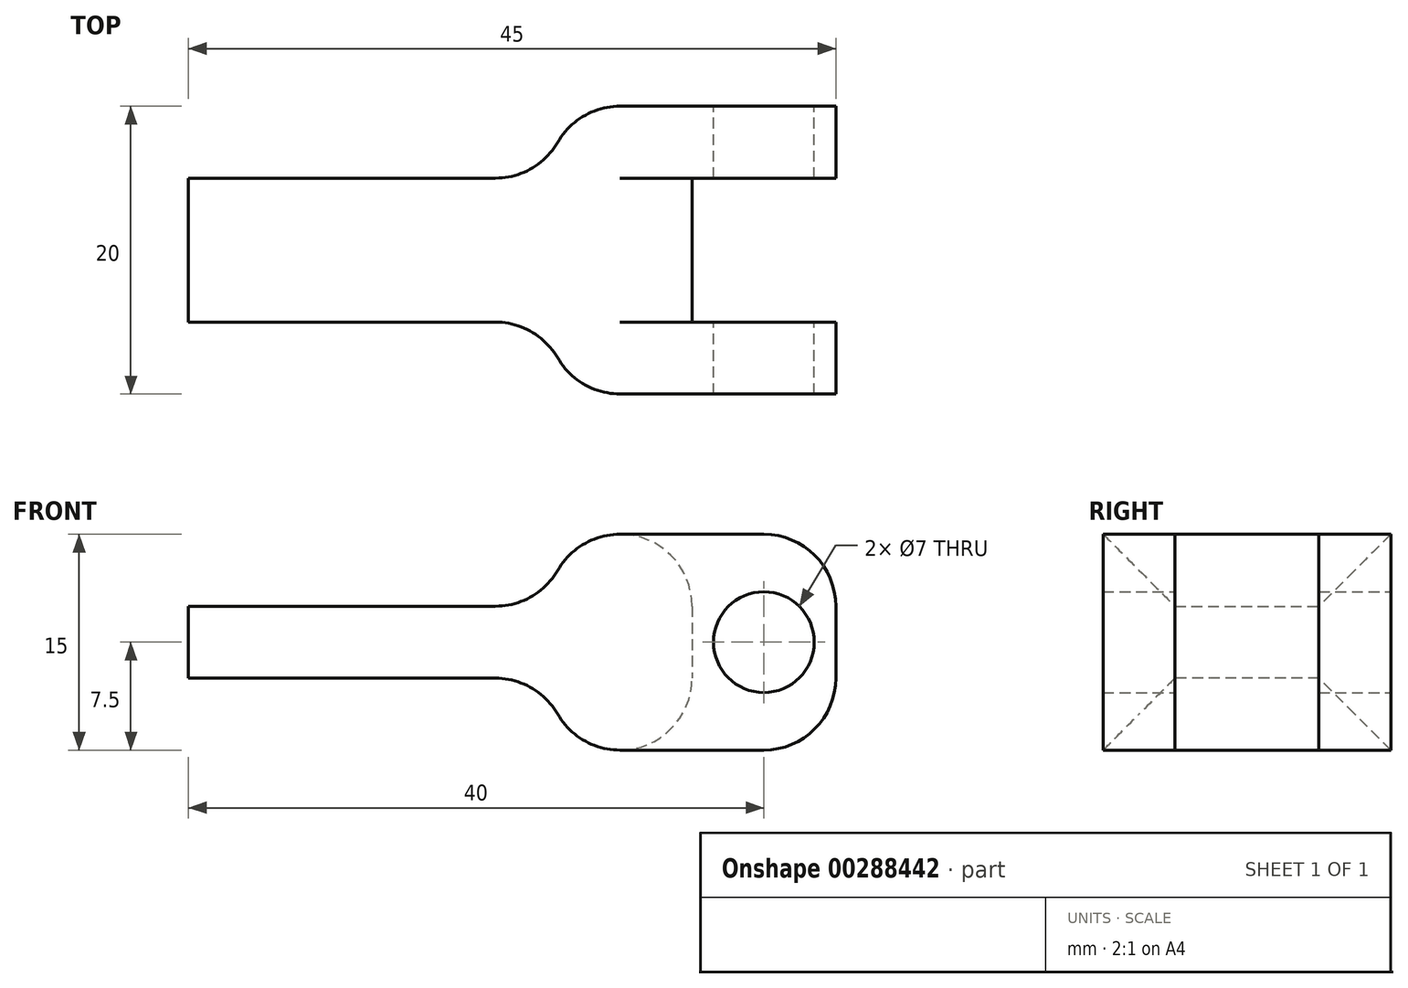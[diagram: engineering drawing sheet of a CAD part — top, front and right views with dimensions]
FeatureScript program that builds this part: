
annotation { "Feature Type Name" : "Feature", "Feature Type Description" : "" }
export const myFeature = defineFeature(function(context is Context, id is Id, definition is map)
    precondition{}
    {
        {
            var Q0;
            Q0=qCreatedBy(makeId("Top.planeOp"),FACE);
            var sketch = newSketch(context, id + "F0", { "sketchPlane" : qUnion([Q0])});
            skLineSegment(sketch, "E0.bottom", {"start": v(-10, 10) * mm, "end": v(10, 10) * mm});
            skLineSegment(sketch, "E0.top", {"start": v(-10, -10) * mm, "end": v(10, -10) * mm});
            skLineSegment(sketch, "E0.left", {"start": v(-10, 10) * mm, "end": v(-10, -10) * mm});
            skLineSegment(sketch, "E0.right", {"start": v(10, 10) * mm, "end": v(10, 5) * mm});
            skPoint(sketch, "E0.middle", {"position": v(0, 0) * mm});
            skLineSegment(sketch, "E1.bottom", {"start": v(0, -5) * mm, "end": v(10, -5) * mm});
            skLineSegment(sketch, "E1.top", {"start": v(0, 5) * mm, "end": v(10, 5) * mm});
            skLineSegment(sketch, "E1.left", {"start": v(0, -5) * mm, "end": v(0, 5) * mm});
            skPoint(sketch, "E1.middle", {"position": v(10, 0) * mm});
            skPoint(sketch, "E1.right.end.orphan", {"position": v(20, 5) * mm});
            skPoint(sketch, "E2.orphan", {"position": v(20, -5) * mm});
            skLineSegment(sketch, "E3.trimOffspring", {"start": v(10, -5) * mm, "end": v(10, -10) * mm});
            skSolve(sketch);
        }
        {
            var Q0;
            Q0 = qSketchRegion(id + "F0", true);
            extrude(context, id + "F1", {"entities" : qUnion([Q0]), "endBound" : BoundingType.SYMMETRIC, "depth" : 15 * mm});
        }
        {
            var Q0;
            Q0=makeQuery(id+"F1.opExtrude","SWEPT_FACE",FACE,{"disambiguationData":[OSD([sQuery(id+"F0.wireOp",EDGE,"E0.bottom")])]});
            var sketch = newSketch(context, id + "F2", { "sketchPlane" : qUnion([Q0])});
            skLineSegment(sketch, "E4", {"start": v(0, 0) * mm, "end": v(-10, 0) * mm, "construction": true});
            skCircle(sketch, "E5", {"center": v(-5, 0) * mm, "radius": 3.5 * mm});
            skSolve(sketch);
        }
        {
            var Q0;
            Q0=sQuery(id+"F2.wireOp",VERTEX,"E5.center");
            var Q1;
            Q1=makeQuery(id+"F1.opExtrude","SWEPT_BODY",BODY,{"disambiguationData":[OSD([sQuery(id+"F0.wireOp",EDGE,"E0.bottom"),sQuery(id+"F0.wireOp",EDGE,"E0.top"),sQuery(id+"F0.wireOp",EDGE,"E0.left"),sQuery(id+"F0.wireOp",EDGE,"E0.right"),sQuery(id+"F0.wireOp",EDGE,"E1.bottom"),sQuery(id+"F0.wireOp",EDGE,"E1.top"),sQuery(id+"F0.wireOp",EDGE,"E1.left"),sQuery(id+"F0.wireOp",EDGE,"E3.trimOffspring")])]});
            hole(context, id + "F3", {"style" : HoleStyle.SIMPLE, "endStyle" : HoleEndStyle.THROUGH, "holeDiameter" : 7 * mm, "tappedDepth" : 12 * mm, "tapClearance" : 3, "locations" : qUnion([Q0]), "scope" : qUnion([Q1])});
        }
        {
            var Q0;
            Q0=makeQuery(id+"F1.opExtrude","CAP_EDGE",EDGE,{"disambiguationData":[OSD([sQuery(id+"F0.wireOp",EDGE,"E0.right")])],"isStart":false});
            var Q1;
            Q1=makeQuery(id+"F1.opExtrude","CAP_EDGE",EDGE,{"disambiguationData":[OSD([sQuery(id+"F0.wireOp",EDGE,"E0.right")])],"isStart":true});
            var Q2;
            Q2=makeQuery(id+"F1.opExtrude","CAP_EDGE",EDGE,{"disambiguationData":[OSD([sQuery(id+"F0.wireOp",EDGE,"E3.trimOffspring")])],"isStart":false});
            var Q3;
            Q3=makeQuery(id+"F1.opExtrude","CAP_EDGE",EDGE,{"disambiguationData":[OSD([sQuery(id+"F0.wireOp",EDGE,"E3.trimOffspring")])],"isStart":true});
            var Q4;
            Q4=makeQuery(id+"F1.opExtrude","SWEPT_FACE",FACE,{"disambiguationData":[OSD([sQuery(id+"F0.wireOp",EDGE,"E0.left")])]});
            fillet(context, id + "F4", {"entities" : qUnion([Q0, Q1, Q2, Q3, Q4]), "radius" : 5 * mm, "tangentPropagation" : true, "allowEdgeOverflow" : false});
        }
        {
            var Q0;
            Q0=makeQuery(id+"F1.opExtrude","CAP_EDGE",EDGE,{"disambiguationData":[OSD([sQuery(id+"F0.wireOp",EDGE,"E1.left")])],"isStart":false});
            var Q1;
            Q1=makeQuery(id+"F1.opExtrude","CAP_EDGE",EDGE,{"disambiguationData":[OSD([sQuery(id+"F0.wireOp",EDGE,"E1.left")])],"isStart":true});
            fillet(context, id + "F5", {"entities" : qUnion([Q0, Q1]), "radius" : 5 * mm, "tangentPropagation" : true, "allowEdgeOverflow" : false});
        }
        {
            var Q0;
            Q0=makeQuery(id+"F1.opExtrude","SWEPT_FACE",FACE,{"disambiguationData":[OSD([sQuery(id+"F0.wireOp",EDGE,"E0.left")])]});
            var sketch = newSketch(context, id + "F6", { "sketchPlane" : qUnion([Q0])});
            skLineSegment(sketch, "E6.bottom", {"start": v(5, 2.5) * mm, "end": v(-5, 2.5) * mm});
            skLineSegment(sketch, "E6.top", {"start": v(5, -2.5) * mm, "end": v(-5, -2.5) * mm});
            skLineSegment(sketch, "E6.left", {"start": v(5, 2.5) * mm, "end": v(5, -2.5) * mm});
            skLineSegment(sketch, "E6.right", {"start": v(-5, 2.5) * mm, "end": v(-5, -2.5) * mm});
            skPoint(sketch, "E6.middle", {"position": v(0, 0) * mm});
            skSolve(sketch);
        }
        {
            var Q0;
            Q0 = qSketchRegion(id + "F6", true);
            extrude(context, id + "F7", {"entities" : qUnion([Q0]), "operationType" : NewBodyOperationType.ADD, "depth" : 25 * mm});
        }
        {
            var Q0;
            {var subQ0=sQuery(id+"F0.wireOp",EDGE,"E0.left");Q0=makeQuery(id+"F7.boolean.opBoolean","MERGE",EDGE,{"derivedFrom":[makeQuery(id+"F4.opFillet","BLEND_EDGE",EDGE,{"blendedFrom":[makeQuery(id+"F1.opExtrude","CAP_EDGE",EDGE,{"disambiguationData":[OSD([subQ0])],"isStart":false}),makeQuery(id+"F1.opExtrude","SWEPT_FACE",FACE,{"disambiguationData":[OSD([subQ0])]})],"blendedInto":[makeQuery(id+"F1.opExtrude","SWEPT_FACE",FACE,{"disambiguationData":[OSD([subQ0])]})]}),makeQuery(id+"F7.opExtrude","CAP_EDGE",EDGE,{"disambiguationData":[OSD([sQuery(id+"F6.wireOp",EDGE,"E6.bottom")])],"isStart":true})]});}
            var Q1;
            {var subQ0=sQuery(id+"F0.wireOp",EDGE,"E0.left");Q1=makeQuery(id+"F7.boolean.opBoolean","MERGE",EDGE,{"derivedFrom":[makeQuery(id+"F4.opFillet","BLEND_EDGE",EDGE,{"blendedFrom":[makeQuery(id+"F1.opExtrude","SWEPT_EDGE",EDGE,{"disambiguationData":[OSD([sQuery(id+"F0.wireOp",EDGE,"E0.top"),subQ0])]}),makeQuery(id+"F1.opExtrude","SWEPT_FACE",FACE,{"disambiguationData":[OSD([subQ0])]})],"blendedInto":[makeQuery(id+"F1.opExtrude","SWEPT_FACE",FACE,{"disambiguationData":[OSD([subQ0])]})]}),makeQuery(id+"F7.opExtrude","CAP_EDGE",EDGE,{"disambiguationData":[OSD([sQuery(id+"F6.wireOp",EDGE,"E6.left")])],"isStart":true})]});}
            var Q2;
            {var subQ0=sQuery(id+"F0.wireOp",EDGE,"E0.left");Q2=makeQuery(id+"F7.boolean.opBoolean","MERGE",EDGE,{"derivedFrom":[makeQuery(id+"F4.opFillet","BLEND_EDGE",EDGE,{"blendedFrom":[makeQuery(id+"F1.opExtrude","CAP_EDGE",EDGE,{"disambiguationData":[OSD([subQ0])],"isStart":true}),makeQuery(id+"F1.opExtrude","SWEPT_FACE",FACE,{"disambiguationData":[OSD([subQ0])]})],"blendedInto":[makeQuery(id+"F1.opExtrude","SWEPT_FACE",FACE,{"disambiguationData":[OSD([subQ0])]})]}),makeQuery(id+"F7.opExtrude","CAP_EDGE",EDGE,{"disambiguationData":[OSD([sQuery(id+"F6.wireOp",EDGE,"E6.top")])],"isStart":true})]});}
            var Q3;
            {var subQ0=sQuery(id+"F0.wireOp",EDGE,"E0.left");Q3=makeQuery(id+"F7.boolean.opBoolean","MERGE",EDGE,{"derivedFrom":[makeQuery(id+"F4.opFillet","BLEND_EDGE",EDGE,{"blendedFrom":[makeQuery(id+"F1.opExtrude","SWEPT_EDGE",EDGE,{"disambiguationData":[OSD([sQuery(id+"F0.wireOp",EDGE,"E0.bottom"),subQ0])]}),makeQuery(id+"F1.opExtrude","SWEPT_FACE",FACE,{"disambiguationData":[OSD([subQ0])]})],"blendedInto":[makeQuery(id+"F1.opExtrude","SWEPT_FACE",FACE,{"disambiguationData":[OSD([subQ0])]})]}),makeQuery(id+"F7.opExtrude","CAP_EDGE",EDGE,{"disambiguationData":[OSD([sQuery(id+"F6.wireOp",EDGE,"E6.right")])],"isStart":true})]});}
            fillet(context, id + "F8", {"entities" : qUnion([Q0, Q1, Q2, Q3]), "radius" : 5 * mm, "tangentPropagation" : true, "allowEdgeOverflow" : false});
        }
    });
